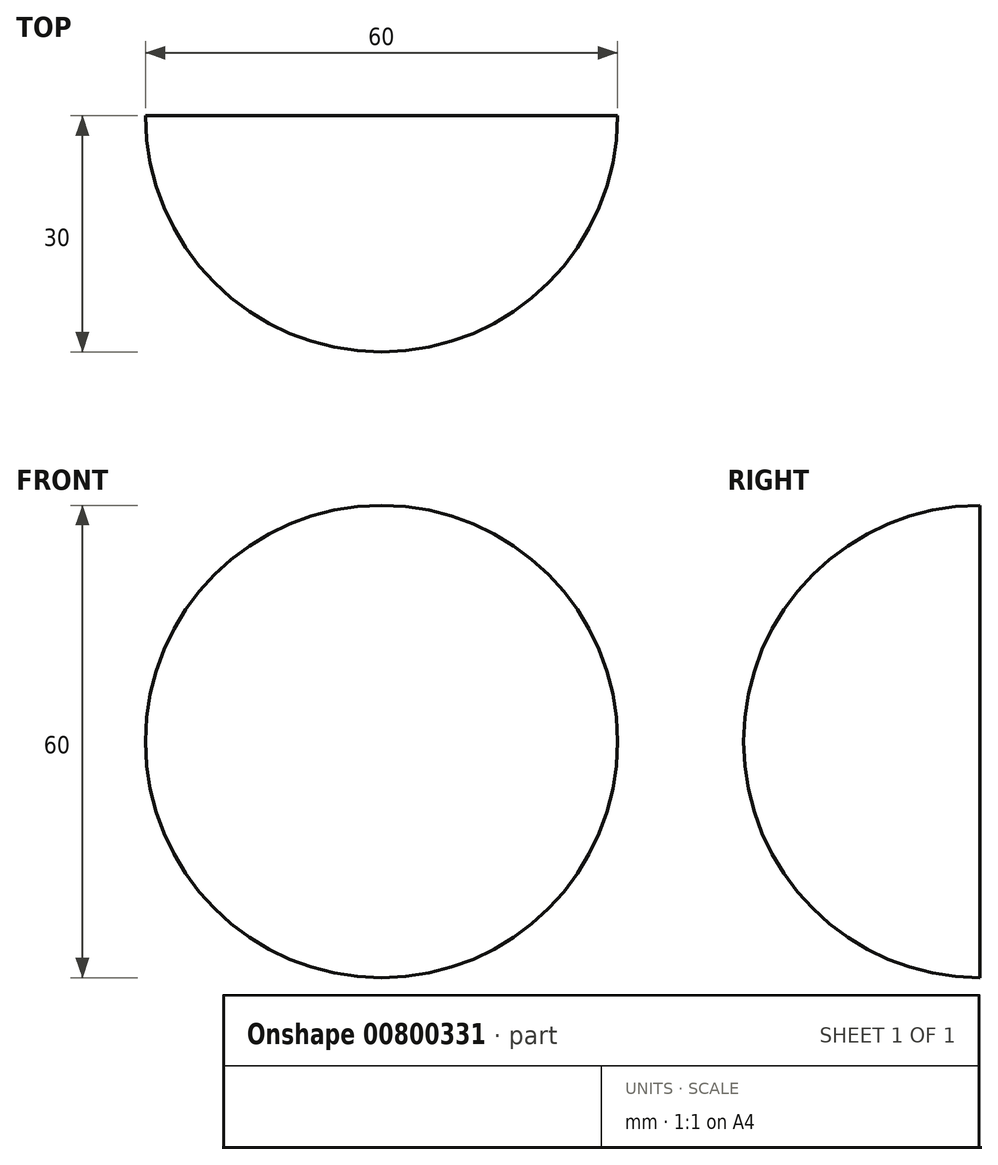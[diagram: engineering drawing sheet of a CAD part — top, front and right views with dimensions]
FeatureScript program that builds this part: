
annotation { "Feature Type Name" : "Feature", "Feature Type Description" : "" }
export const myFeature = defineFeature(function(context is Context, id is Id, definition is map)
    precondition{}
    {
        {
            var Q0;
            Q0=qCreatedBy(makeId("Front.planeOp"),FACE);
            var sketch = newSketch(context, id + "F0", { "sketchPlane" : qUnion([Q0])});
            skArc(sketch, "E0", {"start": v(30, 0) * mm, "mid": v(0, 30) * mm, "end": v(-30, 0) * mm});
            skLineSegment(sketch, "E1", {"start": v(-30, 0) * mm, "end": v(30, 0) * mm});
            skSolve(sketch);
        }
        {
            var Q0;
            Q0 = qSketchRegion(id + "F0", true);
            var Q1;
            Q1=sQuery(id+"F0.wireOp",EDGE,"E1");
            revolve(context, id + "F1", {"surfaceOperationType" : NewSurfaceOperationType.NEW, "entities" : qUnion([Q0]), "axis" : qUnion([Q1]), "revolveType" : RevolveType.ONE_DIRECTION, "angle" : 180 * degree});
        }
    });
